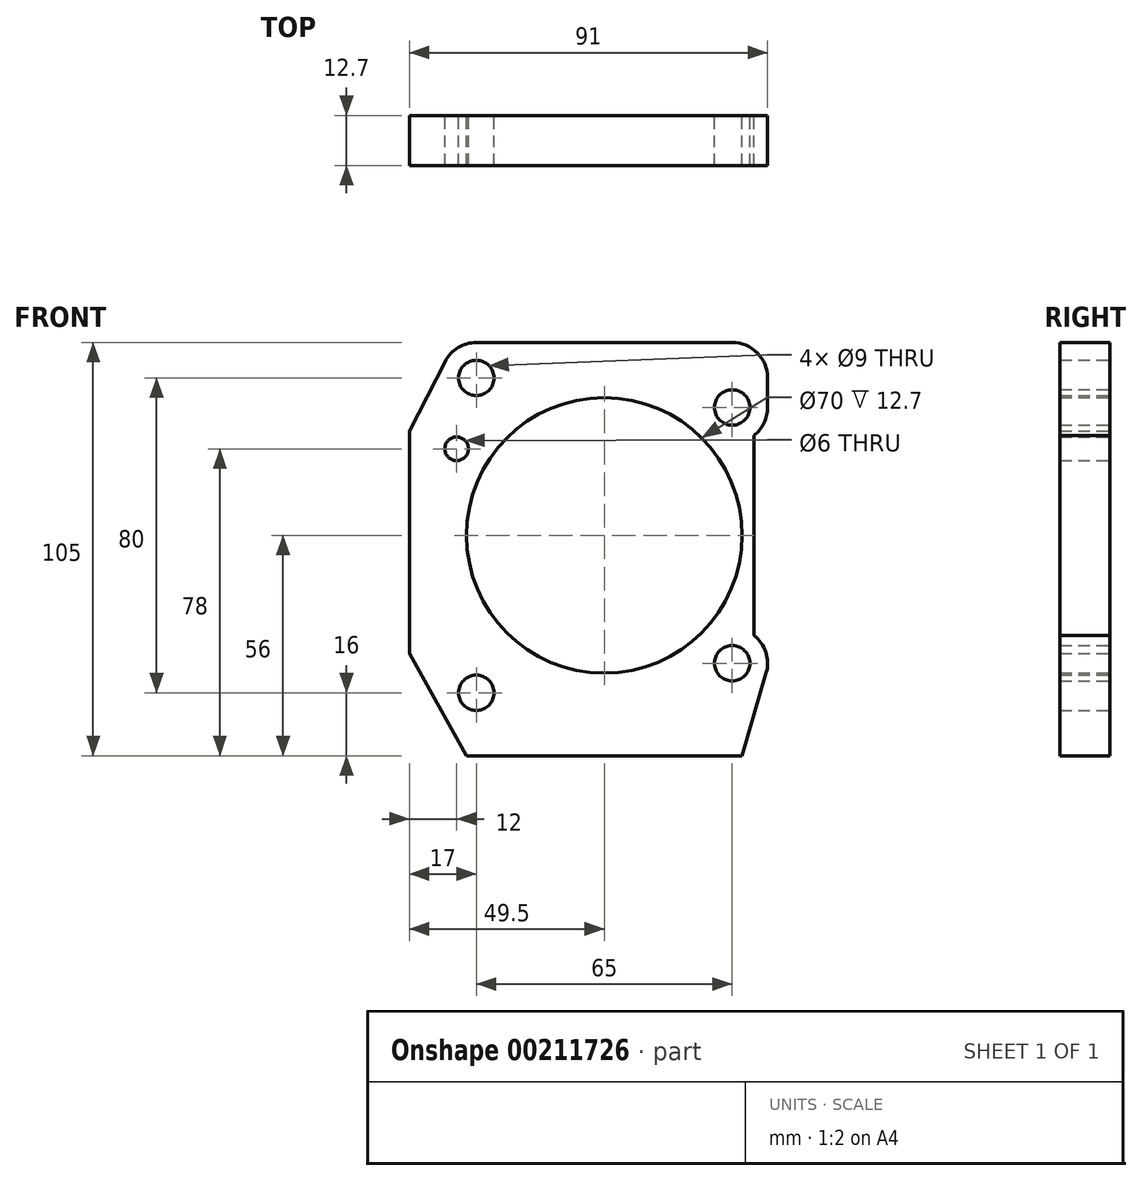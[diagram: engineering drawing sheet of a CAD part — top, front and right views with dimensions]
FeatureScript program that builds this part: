
annotation { "Feature Type Name" : "Feature", "Feature Type Description" : "" }
export const myFeature = defineFeature(function(context is Context, id is Id, definition is map)
    precondition{}
    {
        {
            var Q0;
            Q0=qCreatedBy(makeId("Front.planeOp"),FACE);
            var sketch = newSketch(context, id + "F0", { "sketchPlane" : qUnion([Q0])});
            skCircle(sketch, "E0", {"center": v(0, 0) * mm, "radius": 35 * mm});
            skCircle(sketch, "E1", {"center": v(-32.5, 40) * mm, "radius": 4.5 * mm});
            skCircle(sketch, "E2", {"center": v(32.5, 32.5) * mm, "radius": 4.5 * mm});
            skCircle(sketch, "E3", {"center": v(-32.5, -40) * mm, "radius": 4.5 * mm});
            skCircle(sketch, "E4", {"center": v(32.5, -32.5) * mm, "radius": 4.5 * mm});
            skArc(sketch, "E5", {"start": v(-32.5, 49) * mm, "mid": v(-37.2, 47.68) * mm, "end": v(-40.52, 44.1) * mm});
            skArc(sketch, "E6", {"start": v(38, 25.38) * mm, "mid": v(40.58, 28.53) * mm, "end": v(41.5, 32.5) * mm});
            skArc(sketch, "E7", {"start": v(41.14, -35.01) * mm, "mid": v(41.06, -29.7) * mm, "end": v(38, -25.38) * mm});
            skLineSegment(sketch, "E8", {"start": v(-49.5, 26.5) * mm, "end": v(-49.5, -30) * mm});
            skLineSegment(sketch, "E9", {"start": v(-49.5, 26.5) * mm, "end": v(-40.52, 44.1) * mm});
            skLineSegment(sketch, "E10", {"start": v(-35.05, -56) * mm, "end": v(35.05, -56) * mm});
            skLineSegment(sketch, "E11", {"start": v(35.05, -56) * mm, "end": v(41.14, -35.01) * mm});
            skLineSegment(sketch, "E12", {"start": v(-35.05, -56) * mm, "end": v(-49.5, -30) * mm});
            skLineSegment(sketch, "E13", {"start": v(38, -25.38) * mm, "end": v(38, 25.38) * mm});
            skLineSegment(sketch, "E14", {"start": v(-32.5, 49) * mm, "end": v(32.5, 49) * mm});
            skCircle(sketch, "E15", {"center": v(-37.5, 22) * mm, "radius": 3 * mm});
            skLineSegment(sketch, "E16", {"start": v(41.5, 32.5) * mm, "end": v(41.5, 40) * mm});
            skPoint(sketch, "E17.visualSharp", {"position": v(41.5, 49) * mm});
            skArc(sketch, "E17.filletArc", {"start": v(41.5, 40) * mm, "mid": v(38.86, 46.36) * mm, "end": v(32.5, 49) * mm});
            skSolve(sketch);
        }
        {
            var Q0;
            Q0=makeQuery(id+"F0.imprint","IMPRINT",FACE,{"disambiguationData":[TD([[makeQuery(id+"F0.imprint","IMPRINT",EDGE,{"derivedFrom":sQuery(id+"F0.wireOp",EDGE,"E0")}),-1.0]])]});
            extrude(context, id + "F1", {"entities" : qUnion([Q0]), "endBound" : BoundingType.SYMMETRIC, "depth" : 12.7 * mm, "offsetDistance" : 25.4 * mm});
        }
    });
